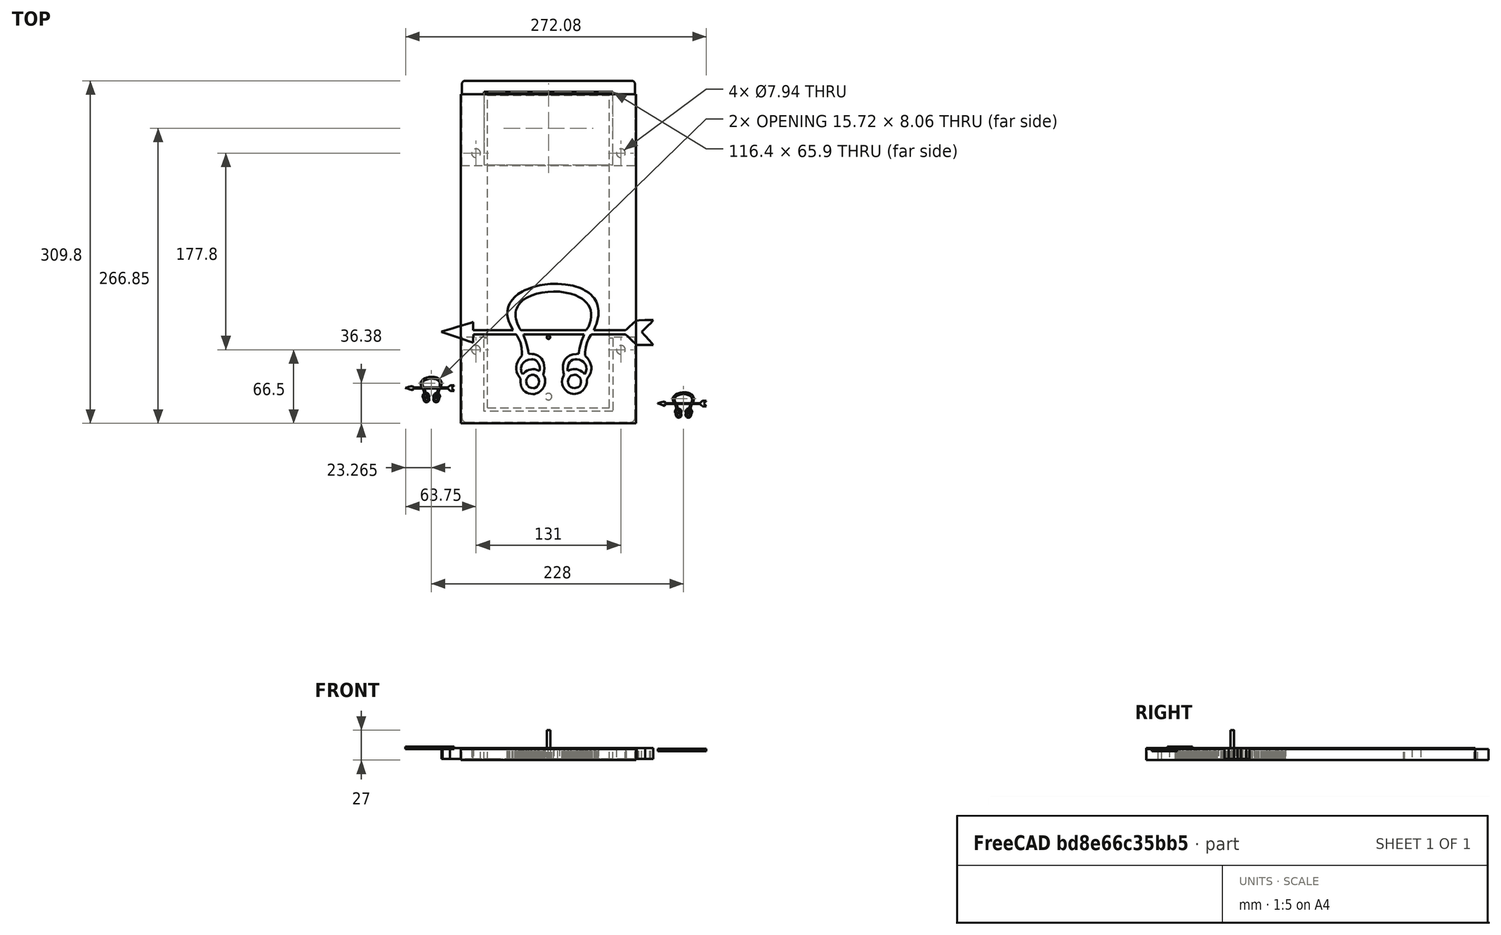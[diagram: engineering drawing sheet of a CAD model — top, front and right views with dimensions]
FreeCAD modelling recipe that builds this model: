
FCSTD DOCUMENT  (FreeCAD 0.22R36958 (Git))
Label: Frame-CNC-center
License: All rights reserved
LicenseURL: http://en.wikipedia.org/wiki/All_rights_reserved
objects: Part::FeaturePython×30, Path::FeaturePython×29, App::DocumentObjectGroup×6, Part::Feature×5, Sketcher::SketchObject×4, PartDesign::Pad×4, PartDesign::Body×4, Part::Part2DObjectPython×2, Part::Extrusion×2, App::FeaturePython×2, Spreadsheet::Sheet×1, Mesh::Feature×1, PartDesign::AdditiveBox×1, PartDesign::SubtractiveCylinder×1, PartDesign::LinearPattern×1
note: 63 computed .brp shape members not serialized (recipe doc carries the construction recipe); baked Part::Feature solids carry a one-line shape summary decoded from their .brp

FEATURE [Part::Part2DObjectPython] ShapeString  # Draft 2D object (typed FeaturePython)
  FontFile = /System/Library/Fonts/Avenir.ttc
  Fuse = false
  Justification = 4
  JustificationReference = 0
  KeepLeftMargin = false
  MakeFace = true
  ObliqueAngle = 0
  Placement = pos=(-68.2,76.9,10) rot=(0,0,1;1.5708rad)
  ScaleToSize = true
  Size = 16
  String = US NAVY
  Tracking = 1
  expr: .Placement.Base.x = -(<<vars>>.width - <<vars>>.top_banner_width) / 2
  expr: .Placement.Base.y = (<<vars>>.length - <<vars>>.template_length) / 2
  expr: .Placement.Base.z = <<vars>>.height
  expr: Size = <<vars>>.font_size
FEATURE [Spreadsheet::Sheet] Spreadsheet  label="vars"
  cells = A1='Length; B1(length)=308.8; C1==B1 / 2; D1='plate hole; E1(plate_hole)=7.9375; A2='Width; B2(width)=156.4; C2=160; D2='plate hole top left distance; E2(plate_hole_vertical)==length / 2 - 177.8 / 2; A3='material length; B3(material_length)=310; D3='plate hole horizontal_right; E3(plate_hole_horizontal_right)==(length - hole_distance_horizontal) / 2; A4='material_width; B4(material_width)=160; D4='plate hole horizontal left; E4(plate_hole_horizontal_left)==length / 2 - 88.9; A5='Font Size; B5(font_size)=16; D5='hole distance horizontal; E5(hole_distance_horizontal)=177.8; A6='Top banner width; B6(top_banner_width)=20; D6='hole distance vertical; E6(hole_distance_vertical)=120.65; A7='Bottom banner witdh; B7(bottom_banner_width)=20; A8='Height; B8(height)=10; A9='Guide hole distance; B9(guide_hole_length)=120; A10='Guide hole width; B10(guide_hole_width)=130; A11='hole distance from edge; B11(hole_distance_from_edge)=20; A12='hole size; B12(hole_size)=6.05; A13='template_length; B13(template_length)=155; A14='reference point; B14(reference_point)==second_cut; C14(second_cut)==(length - template_length) / 2 + template_length; D14(third_cut)==(length - template_length) / 2; E14(first_cut)==length; A15='side_width; B15(side_width)=10; A16='bit size; B16(bit_size)=3.175; A17='bridge width; B17(bridge_width)=1
FEATURE [Part::Part2DObjectPython] ShapeString001  # Draft 2D object (typed FeaturePython)
  FontFile = /System/Library/Fonts/Avenir.ttc
  Fuse = false
  Justification = 4
  JustificationReference = 0
  KeepLeftMargin = false
  MakeFace = true
  ObliqueAngle = 0
  Placement = pos=(68.2,76.9,10) rot=(0,0,1;1.5708rad)
  ScaleToSize = true
  Size = 16
  String = VETERAN
  Tracking = 0
  expr: .Placement.Base.x = (<<vars>>.width - <<vars>>.bottom_banner_width) / 2
  expr: .Placement.Base.y = (<<vars>>.length - <<vars>>.template_length) / 2
  expr: .Placement.Base.z = <<vars>>.height
  expr: Size = <<vars>>.font_size
FEATURE [Mesh::Feature] Sonar_Tech
FEATURE [Part::Feature] Sonar_Tech001
  Placement = pos=(0,0,10) rot=(0,0,1;0rad)
  shape: bbox 191.7 x 99.71 x 10 mm, 1500 faces, 0 solids (baked)
FEATURE [Part::Feature] Shell
  Placement = pos=(0,0,10) rot=(0,0,1;0rad)
  shape: bbox 191.7 x 99.71 x 10 mm, 373 faces, 0 solids (baked)
  expr: .Placement.Base.z = <<vars>>.height
FEATURE [Part::Feature] Scale_solid  label="Scale (Solid)"
  Placement = pos=(13,14,9) rot=(0,0,1;0rad)
  shape: bbox 44.08 x 22.93 x 2.3 mm, 373 faces (baked)
FEATURE [Part::Feature] Scale001_solid  label="Scale001 (Solid)"
  Placement = pos=(0,0,7) rot=(0,0,1;0rad)
  shape: bbox 44.08 x 22.93 x 2.3 mm, 373 faces (baked)
FEATURE [Sketcher::SketchObject] Sketch
  FullyConstrained = true
  MapMode = 5
  expr: Constraints[13] = <<vars>>.width / 2
  expr: Constraints[14] = <<vars>>.width
  expr: Constraints[23] = <<vars>>.top_banner_width
  expr: Constraints[24] = <<vars>>.bottom_banner_width
  expr: Constraints[25] = (<<vars>>.length - <<vars>>.template_length) / 2
  expr: Constraints[29] = <<vars>>.length + 10
  expr: Constraints[30] = (<<vars>>.length - <<vars>>.template_length) / 2 - <<vars>>.side_width - <<vars>>.bridge_width
  expr: Constraints[32] = <<vars>>.plate_hole
  expr: Constraints[33] = <<vars>>.plate_hole
  expr: Constraints[34] = <<vars>>.plate_hole_vertical
  expr: Constraints[35] = <<vars>>.plate_hole_vertical
  expr: Constraints[36] = <<vars>>.plate_hole_horizontal_left
  expr: Constraints[37] = <<vars>>.plate_hole_horizontal_left
  expr: Constraints[38] = <<vars>>.reference_point + 10
  expr: Constraints[39] = <<vars>>.reference_point + <<vars>>.side_width + 10
  sketch-geometry (13):
    g0: LineSegment StartX=78.2 StartY=-5.68e-14 StartZ=0 EndX=-78.2 EndY=-5.68e-14 EndZ=0
    g1: LineSegment StartX=-78.2 StartY=-5.68e-14 StartZ=0 EndX=-78.2 EndY=-72.9 EndZ=0
    g2: ArcOfCircle CenterX=-74.2 CenterY=-72.9 CenterZ=0 NormalX=0 NormalY=0 NormalZ=1 AngleXU=0 Radius=4 StartAngle=3.14159 EndAngle=4.71239
    g3: LineSegment StartX=-74.2 StartY=-76.9 StartZ=0 EndX=74.2 EndY=-76.9 EndZ=0
    g4: ArcOfCircle CenterX=74.2 CenterY=-72.9 CenterZ=0 NormalX=0 NormalY=0 NormalZ=1 AngleXU=0 Radius=4 StartAngle=4.71239 EndAngle=6.28319
    g5: LineSegment StartX=78.2 StartY=-72.9 StartZ=0 EndX=78.2 EndY=-5.68e-14 EndZ=0
    g6: LineSegment StartX=58.2 StartY=-1 StartZ=0 EndX=-58.2 EndY=-1 EndZ=0
    g7: LineSegment StartX=58.2 StartY=-1 StartZ=0 EndX=58.2 EndY=-66.9 EndZ=0
    g8: LineSegment StartX=58.2 StartY=-66.9 StartZ=0 EndX=-58.2 EndY=-66.9 EndZ=0
    g9: LineSegment StartX=-58.2 StartY=-66.9 StartZ=0 EndX=-58.2 EndY=-1 EndZ=0
    g10: GeomPoint X=0 Y=-318.8 Z=0
    g11: Circle CenterX=-65.5 CenterY=-11.4 CenterZ=0 NormalX=0 NormalY=0 NormalZ=1 AngleXU=0 Radius=3.96875
    g12: Circle CenterX=65.5 CenterY=-11.4 CenterZ=0 NormalX=0 NormalY=0 NormalZ=1 AngleXU=0 Radius=3.96875
  constraints (40):
    c: Vertical(g1)
    c: Coincident(g2,g3)
    c: Horizontal(g3)
    c: Tangent(g3,g4) = -1.5708
    c: Coincident(g4,g5)
    c: Vertical(g5)
    c: Horizontal(g8)
    c: Vertical(g9)
    c: Horizontal(g6)
    c: Vertical(g7)
    c: Equal(g2,g4)
    c: Angle(g2) = 1.5708
    c: Angle(g4) = 1.5708
    c: DistanceX(g0,g-1) = 78.2
    c: DistanceX(g0,g5) = 156.4
    c: Equal(g1,g5)
    c: Coincident(g2,g1)
    c: Horizontal(g0)
    c: DistanceX(g2) = -74.2
    c: Coincident(g1,g0)
    c: Coincident(g0,g5)
    c: Coincident(g9,g6)
    c: Coincident(g6,g7)
    c: Distance(g6,g1) = 20
    c: Distance(g6,g5) = 20
    c: Distance(g2,g0) = 76.9
    c: Coincident(g7,g8)
    c: Coincident(g9,g8)
    c: PointOnObject(g10,g-2)
    c: Distance(g-1,g10) = 318.8
    c: DistanceY(g9,g9) = 65.9
    c: DistanceY(g-1,g-1) = 0
    c: Diameter(g11) = 7.9375
    c: Diameter(g12) = 7.9375
    c: DistanceX(g11,g-1) = 65.5
    c: DistanceX(g-1,g12) = 65.5
    c: Distance(g11,g3) = 65.5
    c: Distance(g12,g3) = 65.5
    c: Distance(g10,g3) = 241.9
    c: Distance(g10,g8) = 251.9
FEATURE [PartDesign::Pad] Pad
  Direction = (0,0,1)
  Length = 10
  Length2 = 10
  Profile = -> Sketch
  ReferenceAxis = -> Sketch [N_Axis]
  Suppressed = false
  Type = 0
  expr: Length = <<vars>>.height
FEATURE [PartDesign::AdditiveBox] Box
  AttacherType = Attacher::AttachEngine3D
  AttachmentOffset = pos=(-55.025,-63.725,0) rot=(0,0,1;0rad)
  AttachmentSupport = -> [XY_Plane]
  BaseFeature = -> Pad
  Height = 10
  Length = 110.05
  MapMode = 5
  Placement = pos=(-55.025,-63.725,0) rot=(0,0,1;0rad)
  Suppressed = false
  Width = 282.45
  expr: .AttachmentOffset.Base.x = -<<vars>>.width / 2 + <<vars>>.top_banner_width + <<vars>>.bit_size
  expr: .AttachmentOffset.Base.y = <<vars>>.reference_point - <<vars>>.length + <<vars>>.side_width + <<vars>>.bit_size
  expr: Height = <<vars>>.height
  expr: Length = <<vars>>.width - <<vars>>.top_banner_width - <<vars>>.bottom_banner_width - <<vars>>.bit_size * 2
  expr: Width = <<vars>>.length - <<vars>>.side_width * 2 - <<vars>>.bit_size * 2
FEATURE [Sketcher::SketchObject] Sketch001
  FullyConstrained = true
  MapMode = 5
  expr: Constraints[18] = <<vars>>.width
  expr: Constraints[23] = <<vars>>.top_banner_width
  expr: Constraints[24] = <<vars>>.bottom_banner_width
  expr: Constraints[25] = -<<vars>>.width / 2
  expr: Constraints[26] = (<<vars>>.length - <<vars>>.template_length) / 2
  expr: Constraints[28] = <<vars>>.plate_hole
  expr: Constraints[30] = <<vars>>.plate_hole_vertical
  expr: Constraints[31] = <<vars>>.plate_hole_vertical
  expr: Constraints[32] = <<vars>>.plate_hole_horizontal_right
  expr: Constraints[34] = <<vars>>.length + <<vars>>.reference_point
  expr: Constraints[35] = <<vars>>.length
  expr: Constraints[36] = <<vars>>.length - <<vars>>.side_width + <<vars>>.reference_point
  expr: Constraints[37] = <<vars>>.length - (<<vars>>.length - <<vars>>.template_length) / 2 + <<vars>>.bridge_width + <<vars>>.reference_point
  sketch-geometry (13):
    g0: LineSegment StartX=-78.2 StartY=155 StartZ=0 EndX=-78.2 EndY=228.9 EndZ=0
    g1: ArcOfCircle CenterX=-75.2 CenterY=228.9 CenterZ=0 NormalX=0 NormalY=0 NormalZ=1 AngleXU=0 Radius=3 StartAngle=1.5708 EndAngle=3.14159
    g2: LineSegment StartX=-75.2 StartY=231.9 StartZ=0 EndX=75.2 EndY=231.9 EndZ=0
    g3: ArcOfCircle CenterX=75.2 CenterY=228.9 CenterZ=0 NormalX=0 NormalY=0 NormalZ=1 AngleXU=0 Radius=3 StartAngle=5.988e-13 EndAngle=1.5708
    g4: LineSegment StartX=78.2 StartY=228.9 StartZ=0 EndX=78.2 EndY=155 EndZ=0
    g5: LineSegment StartX=78.2 StartY=155 StartZ=0 EndX=-78.2 EndY=155 EndZ=0
    g6: LineSegment StartX=-58.2 StartY=156 StartZ=0 EndX=58.2 EndY=156 EndZ=0
    g7: LineSegment StartX=58.2 StartY=156 StartZ=0 EndX=58.2 EndY=221.9 EndZ=0
    g8: LineSegment StartX=58.2 StartY=221.9 StartZ=0 EndX=-58.2 EndY=221.9 EndZ=0
    g9: LineSegment StartX=-58.2 StartY=221.9 StartZ=0 EndX=-58.2 EndY=156 EndZ=0
    g10: Circle CenterX=-65.5 CenterY=166.4 CenterZ=0 NormalX=0 NormalY=0 NormalZ=1 AngleXU=0 Radius=3.96875
    g11: Circle CenterX=65.5 CenterY=166.4 CenterZ=0 NormalX=0 NormalY=0 NormalZ=1 AngleXU=0 Radius=3.96875
    g12: GeomPoint X=0 Y=-308.8 Z=0
  constraints (38):
    c: Tangent(g0,g1) = 1.5708
    c: Coincident(g1,g2)
    c: Horizontal(g2)
    c: Tangent(g2,g3) = 1.5708
    c: Coincident(g3,g4)
    c: Vertical(g4)
    c: Coincident(g4,g5)
    c: Coincident(g5,g0)
    c: Horizontal(g5)
    c: Coincident(g6,g7)
    c: Coincident(g7,g8)
    c: Coincident(g8,g9)
    c: Coincident(g9,g6)
    c: Horizontal(g6)
    c: Horizontal(g8)
    c: Vertical(g7)
    c: Vertical(g9)
    c: Vertical(g0)
    c: DistanceX(g5,g5) = 156.4
    c: Angle(g1) = 1.5708
    c: Angle(g3) = 1.5708
    c: Diameter(g1) = 6
    c: Diameter(g3) = 6
    c: Distance(g6,g0) = 20
    c: Distance(g6,g4) = 20
    c: DistanceX(g-2,g0) = -78.2
    c: Distance(g4,g2) = 76.9
    c: Equal(g11,g10)
    c: Diameter(g11) = 7.9375
    c: Horizontal(g10,g11)
    c: DistanceX(g10,g-1) = 65.5
    c: DistanceX(g-1,g11) = 65.5
    c: Distance(g10,g2) = 65.5
    c: PointOnObject(g12,g-2)
    c: Distance(g12,g2) = 540.7
    c: DistanceY(g12,g-1) = 308.8
    c: Distance(g12,g8) = 530.7
    c: Distance(g12,g6) = 464.8
FEATURE [PartDesign::Pad] Pad001
  Direction = (0,0,1)
  Length = 10
  Length2 = 10
  Profile = -> Sketch001
  ReferenceAxis = -> Sketch001 [N_Axis]
  Suppressed = false
  Type = 0
  expr: Length = <<vars>>.height
FEATURE [PartDesign::Body] Body001
  Group = -> [Sketch001,Pad001]
  Origin = -> Origin001
  Tip = -> Pad001
FEATURE [Part::Feature] Sonar_Tech001_solid  label="Sonar_Tech001 (Solid)"
  Placement = pos=(0,0,1) rot=(0,0,1;0rad)
  shape: bbox 191.7 x 99.71 x 10 mm, 1500 faces (baked)
FEATURE [Part::Extrusion] Extrude
  Base = -> ShapeString
  Dir = (0,0,1)
  DirMode = 2
  FaceMakerClass = Part::FaceMakerBullseye
  LengthFwd = 2
  LengthRev = 0
  Solid = false
  Symmetric = true
FEATURE [Part::Extrusion] Extrude001
  Base = -> ShapeString001
  Dir = (0,0,1)
  DirMode = 2
  FaceMakerClass = Part::FaceMakerBullseye
  LengthFwd = 2
  LengthRev = 0
  Solid = false
  Symmetric = true
FEATURE [Sketcher::SketchObject] Sketch002
  FullyConstrained = true
  MapMode = 5
  expr: Constraints[10] = -<<vars>>.width / 2
  expr: Constraints[12] = <<vars>>.length
  expr: Constraints[13] = (<<vars>>.length - <<vars>>.template_length) / 2 + <<vars>>.reference_point
  expr: Constraints[8] = <<vars>>.top_banner_width
  expr: Constraints[9] = <<vars>>.template_length
  sketch-geometry (5):
    g0: LineSegment StartX=-78.2 StartY=155 StartZ=0 EndX=-78.2 EndY=2.84e-14 EndZ=0
    g1: LineSegment StartX=-78.2 StartY=2.13e-14 StartZ=0 EndX=-58.2 EndY=2.13e-14 EndZ=0
    g2: LineSegment StartX=-58.2 StartY=2.13e-14 StartZ=0 EndX=-58.2 EndY=155 EndZ=0
    g3: LineSegment StartX=-58.2 StartY=155 StartZ=0 EndX=-78.2 EndY=155 EndZ=0
    g4: GeomPoint X=0 Y=-308.8 Z=0
  constraints (14):
    c: Coincident(g0,g1)
    c: Coincident(g1,g2)
    c: Coincident(g2,g3)
    c: Coincident(g3,g0)
    c: Vertical(g0)
    c: Vertical(g2)
    c: Horizontal(g1)
    c: Horizontal(g3)
    c: DistanceX(g3,g3) = 20
    c: DistanceY(g0,g0) = 155
    c: DistanceX(g-2,g0) = -78.2
    c: PointOnObject(g4,g-2)
    c: DistanceY(g4,g-1) = 308.8
    c: DistanceY(g4,g1) = 308.8
FEATURE [PartDesign::Pad] Pad002
  Direction = (0,0,1)
  Length = 10
  Length2 = 10
  Profile = -> Sketch002
  ReferenceAxis = -> Sketch002 [N_Axis]
  Suppressed = false
  Type = 0
  expr: Length = <<vars>>.height
FEATURE [PartDesign::Body] Body002
  Group = -> [Sketch002,Pad002]
  Origin = -> Origin002
  Tip = -> Pad002
FEATURE [Sketcher::SketchObject] Sketch003
  FullyConstrained = true
  MapMode = 5
  expr: Constraints[11] = <<vars>>.length
  expr: Constraints[12] = <<vars>>.width / 2
  expr: Constraints[13] = (<<vars>>.length - <<vars>>.template_length) / 2 + <<vars>>.reference_point
  expr: Constraints[8] = <<vars>>.bottom_banner_width
  expr: Constraints[9] = <<vars>>.template_length
  sketch-geometry (5):
    g0: LineSegment StartX=58.2 StartY=155 StartZ=0 EndX=58.2 EndY=0 EndZ=0
    g1: LineSegment StartX=58.2 StartY=1.42e-14 StartZ=0 EndX=78.2 EndY=1.42e-14 EndZ=0
    g2: LineSegment StartX=78.2 StartY=1.42e-14 StartZ=0 EndX=78.2 EndY=155 EndZ=0
    g3: LineSegment StartX=78.2 StartY=155 StartZ=0 EndX=58.2 EndY=155 EndZ=0
    g4: GeomPoint X=0 Y=-308.8 Z=0
  constraints (14):
    c: Coincident(g0,g1)
    c: Coincident(g1,g2)
    c: Coincident(g2,g3)
    c: Coincident(g3,g0)
    c: Vertical(g0)
    c: Vertical(g2)
    c: Horizontal(g1)
    c: Horizontal(g3)
    c: DistanceX(g3,g3) = 20
    c: DistanceY(g2,g2) = 155
    c: PointOnObject(g4,g-2)
    c: DistanceY(g4,g-1) = 308.8
    c: DistanceX(g-1,g2) = 78.2
    c: DistanceY(g4,g0) = 308.8
FEATURE [PartDesign::Pad] Pad003
  Direction = (0,0,1)
  Length = 10
  Length2 = 10
  Profile = -> Sketch003
  ReferenceAxis = -> Sketch003 [N_Axis]
  Suppressed = false
  Type = 0
  expr: Length = <<vars>>.height
FEATURE [PartDesign::Body] Body003
  Group = -> [Sketch003,Pad003]
  Origin = -> Origin003
  Tip = -> Pad003
FEATURE [PartDesign::SubtractiveCylinder] Cylinder
  Angle = 360
  AttacherType = Attacher::AttachEngine3D
  AttachmentOffset = pos=(55.025,10,-10) rot=(0,0,1;0rad)
  AttachmentSupport = -> [Box]
  BaseFeature = -> Box
  FirstAngle = 0
  Height = 10
  MapMode = 5
  Placement = pos=(0,-53.725,0) rot=(0,0,1;0rad)
  Radius = 3.03
  SecondAngle = 0
  Suppressed = false
  expr: .AttachmentOffset.Base.x = Box.Length / 2
  expr: .AttachmentOffset.Base.y = <<vars>>.side_width
  expr: .AttachmentOffset.Base.z = -Height
  expr: Height = <<vars>>.height
  expr: Radius = 3.03
FEATURE [PartDesign::LinearPattern] LinearPattern
  BaseFeature = -> Cylinder
  Direction = -> Y_Axis
  Length = 75.91
  Mode = 1
  Occurrences = 2
  Offset = 75.91
  Originals = -> [Cylinder]
  Placement = pos=(0,-53.725,0) rot=(0,0,1;0rad)
  Suppressed = false
  expr: Offset = 75.91 mm
FEATURE [PartDesign::Body] Body
  Group = -> [Sketch,Pad,Box,Cylinder,LinearPattern]
  Origin = -> Origin
  Tip = -> Cylinder
FEATURE [App::FeaturePython] SetupSheet  # Path/CAM operation (typed FeaturePython)
  ClearanceHeightExpression = OpStockZMax+SetupSheet.ClearanceHeightOffset
  ClearanceHeightOffset = 5
  CoolantMode = 0
  CoolantModes = None | Flood | Mist
  FinalDepthExpression = OpFinalDepth
  HorizRapid = 0
  SafeHeightExpression = OpStockZMax+SetupSheet.SafeHeightOffset
  SafeHeightOffset = 3
  StartDepthExpression = OpStartDepth
  StepDownExpression = OpToolDiameter
  VertRapid = 0
FEATURE [Part::FeaturePython] Clone  label="Model-Body"  # Draft clone (typed FeaturePython)
  AttacherType = Attacher::AttachEngine3D
  Fuse = false
  Objects = -> [Body]
  PathResource = Model
  Scale = (1,1,1)
FEATURE [Part::FeaturePython] Clone001  label="Model-Extrude"  # Draft clone (typed FeaturePython)
  AttacherType = Attacher::AttachEngine3D
  Fuse = false
  Objects = -> [Extrude]
  PathResource = Model
  Scale = (1,1,1)
FEATURE [Part::FeaturePython] Clone002  label="Model-Extrude001"  # Draft clone (typed FeaturePython)
  AttacherType = Attacher::AttachEngine3D
  Fuse = false
  Objects = -> [Extrude001]
  PathResource = Model
  Scale = (1,1,1)
FEATURE [App::DocumentObjectGroup] Model
  Group = -> [Clone,Clone001,Clone002]
FEATURE [Part::FeaturePython] ToolBit  label="0.8mm_Endmill004"  # Path/CAM toolbit (typed FeaturePython)
  BitPropertyNames = Chipload | CuttingEdgeHeight | Diameter | Flutes | Length | Material | ShankDiameter | SpindleDirection
  BitShape = /private/var/folders/4z/cpn_82wx3qz0m4lfqxz9fps80000gn/T/AppTranslocation/590B87E8-BEDD-40D1-A770-7063B047F674/d/FreeCAD.app/Contents/Resources/Mod/CAM/Tools/Shape/endmill.fcstd
  Chipload = 0
  CuttingEdgeHeight = 10
  Diameter = 0.8
  Flutes = 0
  Length = 27
  Material = 0
  ShankDiameter = 3.17
  ShapeName = endmill
  SpindleDirection = 0
FEATURE [Path::FeaturePython] __8mm_Endmill001  label="0.8mm_Endmill002"  # Path/CAM operation (typed FeaturePython)
  HorizFeed = 3.33333
  HorizRapid = 0
  SpindleDir = 0
  SpindleSpeed = 2000
  Tool = -> ToolBit
  ToolNumber = 2
  VertFeed = 3.33333
  VertRapid = 0
  expr: HorizRapid = SetupSheet.HorizRapid
  expr: VertRapid = SetupSheet.VertRapid
FEATURE [Part::FeaturePython] ToolBit001  label="1.0mm_Endmill003"  # Path/CAM toolbit (typed FeaturePython)
  BitPropertyNames = Chipload | CuttingEdgeHeight | Diameter | Flutes | Length | Material | ShankDiameter | SpindleDirection
  BitShape = /private/var/folders/4z/cpn_82wx3qz0m4lfqxz9fps80000gn/T/AppTranslocation/590B87E8-BEDD-40D1-A770-7063B047F674/d/FreeCAD.app/Contents/Resources/Mod/CAM/Tools/Shape/endmill.fcstd
  Chipload = 0
  CuttingEdgeHeight = 10
  Diameter = 1
  Flutes = 0
  Length = 27
  Material = 0
  ShankDiameter = 3.17
  ShapeName = endmill
  SpindleDirection = 0
FEATURE [Path::FeaturePython] __0mm_Endmill001  label="1.0mm_Endmill002"  # Path/CAM operation (typed FeaturePython)
  HorizFeed = 3.33333
  HorizRapid = 0
  SpindleDir = 0
  SpindleSpeed = 2000
  Tool = -> ToolBit001
  ToolNumber = 3
  VertFeed = 3.33333
  VertRapid = 0
  expr: HorizRapid = SetupSheet.HorizRapid
  expr: VertRapid = SetupSheet.VertRapid
FEATURE [Part::FeaturePython] ToolBit002  label="1.2mm_endmill003"  # Path/CAM toolbit (typed FeaturePython)
  BitPropertyNames = Chipload | CuttingEdgeHeight | Diameter | Flutes | Length | Material | ShankDiameter | SpindleDirection
  BitShape = /private/var/folders/4z/cpn_82wx3qz0m4lfqxz9fps80000gn/T/AppTranslocation/590B87E8-BEDD-40D1-A770-7063B047F674/d/FreeCAD.app/Contents/Resources/Mod/CAM/Tools/Shape/endmill.fcstd
  Chipload = 0
  CuttingEdgeHeight = 10
  Diameter = 1.2
  Flutes = 0
  Length = 27
  Material = 0
  ShankDiameter = 3.13
  ShapeName = endmill
  SpindleDirection = 0
FEATURE [Path::FeaturePython] __2mm_endmill001  label="1.2mm_endmill002"  # Path/CAM operation (typed FeaturePython)
  HorizFeed = 3.33333
  HorizRapid = 0
  SpindleDir = 0
  SpindleSpeed = 2000
  Tool = -> ToolBit002
  ToolNumber = 4
  VertFeed = 3.33333
  VertRapid = 0
  expr: HorizRapid = SetupSheet.HorizRapid
  expr: VertRapid = SetupSheet.VertRapid
FEATURE [Part::FeaturePython] ToolBit003  label="1.4mm_Endmill003"  # Path/CAM toolbit (typed FeaturePython)
  BitPropertyNames = Chipload | CuttingEdgeHeight | Diameter | Flutes | Length | Material | ShankDiameter | SpindleDirection
  BitShape = /private/var/folders/4z/cpn_82wx3qz0m4lfqxz9fps80000gn/T/AppTranslocation/590B87E8-BEDD-40D1-A770-7063B047F674/d/FreeCAD.app/Contents/Resources/Mod/CAM/Tools/Shape/endmill.fcstd
  Chipload = 0
  CuttingEdgeHeight = 10
  Diameter = 1.4
  Flutes = 0
  Length = 27
  Material = 0
  ShankDiameter = 3.17
  ShapeName = endmill
  SpindleDirection = 0
FEATURE [Path::FeaturePython] __4mm_Endmill001  label="1.4mm_Endmill002"  # Path/CAM operation (typed FeaturePython)
  HorizFeed = 3.33333
  HorizRapid = 0
  SpindleDir = 0
  SpindleSpeed = 2000
  Tool = -> ToolBit003
  ToolNumber = 5
  VertFeed = 3.33333
  VertRapid = 0
  expr: HorizRapid = SetupSheet.HorizRapid
  expr: VertRapid = SetupSheet.VertRapid
FEATURE [Part::FeaturePython] ToolBit004  label="1.8mm_Endmill"  # Path/CAM toolbit (typed FeaturePython)
  BitPropertyNames = Chipload | CuttingEdgeHeight | Diameter | Flutes | Length | Material | ShankDiameter | SpindleDirection
  BitShape = /private/var/folders/4z/cpn_82wx3qz0m4lfqxz9fps80000gn/T/AppTranslocation/590B87E8-BEDD-40D1-A770-7063B047F674/d/FreeCAD.app/Contents/Resources/Mod/CAM/Tools/Shape/endmill.fcstd
  Chipload = 0
  CuttingEdgeHeight = 10
  Diameter = 1.8
  Flutes = 0
  Length = 27
  Material = 0
  ShankDiameter = 3.17
  ShapeName = endmill
  SpindleDirection = 0
FEATURE [Path::FeaturePython] __8mm_Endmill002  label="1.8mm_Endmill001"  # Path/CAM operation (typed FeaturePython)
  HorizFeed = 3.33333
  HorizRapid = 0
  SpindleDir = 0
  SpindleSpeed = 2000
  Tool = -> ToolBit004
  ToolNumber = 7
  VertFeed = 3.33333
  VertRapid = 0
  expr: HorizRapid = SetupSheet.HorizRapid
  expr: VertRapid = SetupSheet.VertRapid
FEATURE [Part::FeaturePython] ToolBit005  label="2.0mm_Endmill"  # Path/CAM toolbit (typed FeaturePython)
  BitPropertyNames = Chipload | CuttingEdgeHeight | Diameter | Flutes | Length | Material | ShankDiameter | SpindleDirection
  BitShape = /private/var/folders/4z/cpn_82wx3qz0m4lfqxz9fps80000gn/T/AppTranslocation/590B87E8-BEDD-40D1-A770-7063B047F674/d/FreeCAD.app/Contents/Resources/Mod/CAM/Tools/Shape/endmill.fcstd
  Chipload = 0
  CuttingEdgeHeight = 10
  Diameter = 2
  Flutes = 0
  Length = 27
  Material = 0
  ShankDiameter = 3.17
  ShapeName = endmill
  SpindleDirection = 0
FEATURE [Path::FeaturePython] __0mm_Endmill002  label="2.0mm_Endmill001"  # Path/CAM operation (typed FeaturePython)
  HorizFeed = 3.33333
  HorizRapid = 0
  SpindleDir = 0
  SpindleSpeed = 2000
  Tool = -> ToolBit005
  ToolNumber = 8
  VertFeed = 3.33333
  VertRapid = 0
  expr: HorizRapid = SetupSheet.HorizRapid
  expr: VertRapid = SetupSheet.VertRapid
FEATURE [Part::FeaturePython] ToolBit006  label="2.2mm_Endmill"  # Path/CAM toolbit (typed FeaturePython)
  BitPropertyNames = Chipload | CuttingEdgeHeight | Diameter | Flutes | Length | Material | ShankDiameter | SpindleDirection
  BitShape = /private/var/folders/4z/cpn_82wx3qz0m4lfqxz9fps80000gn/T/AppTranslocation/590B87E8-BEDD-40D1-A770-7063B047F674/d/FreeCAD.app/Contents/Resources/Mod/CAM/Tools/Shape/endmill.fcstd
  Chipload = 0
  CuttingEdgeHeight = 10
  Diameter = 2.2
  Flutes = 0
  Length = 27
  Material = 0
  ShankDiameter = 3.17
  ShapeName = endmill
  SpindleDirection = 0
FEATURE [Path::FeaturePython] __2mm_Endmill  label="2.2mm_Endmill001"  # Path/CAM operation (typed FeaturePython)
  HorizFeed = 3.33333
  HorizRapid = 0
  SpindleDir = 0
  SpindleSpeed = 2000
  Tool = -> ToolBit006
  ToolNumber = 9
  VertFeed = 3.33333
  VertRapid = 0
  expr: HorizRapid = SetupSheet.HorizRapid
  expr: VertRapid = SetupSheet.VertRapid
FEATURE [Part::FeaturePython] ToolBit007  label="2.4mm_Endmill"  # Path/CAM toolbit (typed FeaturePython)
  BitPropertyNames = Chipload | CuttingEdgeHeight | Diameter | Flutes | Length | Material | ShankDiameter | SpindleDirection
  BitShape = /private/var/folders/4z/cpn_82wx3qz0m4lfqxz9fps80000gn/T/AppTranslocation/590B87E8-BEDD-40D1-A770-7063B047F674/d/FreeCAD.app/Contents/Resources/Mod/CAM/Tools/Shape/endmill.fcstd
  Chipload = 0
  CuttingEdgeHeight = 10
  Diameter = 2.4
  Flutes = 0
  Length = 27
  Material = 0
  ShankDiameter = 3.17
  ShapeName = endmill
  SpindleDirection = 0
FEATURE [Path::FeaturePython] __4mm_Endmill002  label="2.4mm_Endmill001"  # Path/CAM operation (typed FeaturePython)
  HorizFeed = 3.33333
  HorizRapid = 0
  SpindleDir = 0
  SpindleSpeed = 2000
  Tool = -> ToolBit007
  ToolNumber = 10
  VertFeed = 3.33333
  VertRapid = 0
  expr: HorizRapid = SetupSheet.HorizRapid
  expr: VertRapid = SetupSheet.VertRapid
FEATURE [Part::FeaturePython] ToolBit008  label="2.6mm_Endmill"  # Path/CAM toolbit (typed FeaturePython)
  BitPropertyNames = Chipload | CuttingEdgeHeight | Diameter | Flutes | Length | Material | ShankDiameter | SpindleDirection
  BitShape = /private/var/folders/4z/cpn_82wx3qz0m4lfqxz9fps80000gn/T/AppTranslocation/590B87E8-BEDD-40D1-A770-7063B047F674/d/FreeCAD.app/Contents/Resources/Mod/CAM/Tools/Shape/endmill.fcstd
  Chipload = 0
  CuttingEdgeHeight = 10
  Diameter = 2.6
  Flutes = 0
  Length = 27
  Material = 0
  ShankDiameter = 3.17
  ShapeName = endmill
  SpindleDirection = 0
FEATURE [Path::FeaturePython] __6mm_Endmill  label="2.6mm_Endmill001"  # Path/CAM operation (typed FeaturePython)
  HorizFeed = 3.33333
  HorizRapid = 0
  SpindleDir = 0
  SpindleSpeed = 2000
  Tool = -> ToolBit008
  ToolNumber = 11
  VertFeed = 3.33333
  VertRapid = 0
  expr: HorizRapid = SetupSheet.HorizRapid
  expr: VertRapid = SetupSheet.VertRapid
FEATURE [Part::FeaturePython] ToolBit009  label="2.8mm_Endmill"  # Path/CAM toolbit (typed FeaturePython)
  BitPropertyNames = Chipload | CuttingEdgeHeight | Diameter | Flutes | Length | Material | ShankDiameter | SpindleDirection
  BitShape = /private/var/folders/4z/cpn_82wx3qz0m4lfqxz9fps80000gn/T/AppTranslocation/590B87E8-BEDD-40D1-A770-7063B047F674/d/FreeCAD.app/Contents/Resources/Mod/CAM/Tools/Shape/endmill.fcstd
  Chipload = 0
  CuttingEdgeHeight = 10
  Diameter = 2.8
  Flutes = 0
  Length = 27
  Material = 0
  ShankDiameter = 3.17
  ShapeName = endmill
  SpindleDirection = 0
FEATURE [Path::FeaturePython] __8mm_Endmill003  label="2.8mm_Endmill001"  # Path/CAM operation (typed FeaturePython)
  HorizFeed = 3.33333
  HorizRapid = 0
  SpindleDir = 0
  SpindleSpeed = 2000
  Tool = -> ToolBit009
  ToolNumber = 12
  VertFeed = 3.33333
  VertRapid = 0
  expr: HorizRapid = SetupSheet.HorizRapid
  expr: VertRapid = SetupSheet.VertRapid
FEATURE [Part::FeaturePython] ToolBit010  label="3.0mm_Endmill"  # Path/CAM toolbit (typed FeaturePython)
  BitPropertyNames = Chipload | CuttingEdgeHeight | Diameter | Flutes | Length | Material | ShankDiameter | SpindleDirection
  BitShape = /private/var/folders/4z/cpn_82wx3qz0m4lfqxz9fps80000gn/T/AppTranslocation/590B87E8-BEDD-40D1-A770-7063B047F674/d/FreeCAD.app/Contents/Resources/Mod/CAM/Tools/Shape/endmill.fcstd
  Chipload = 0
  CuttingEdgeHeight = 10
  Diameter = 3
  Flutes = 0
  Length = 27
  Material = 0
  ShankDiameter = 3.17
  ShapeName = endmill
  SpindleDirection = 0
FEATURE [Path::FeaturePython] __0mm_Endmill003  label="3.0mm_Endmill001"  # Path/CAM operation (typed FeaturePython)
  HorizFeed = 3.33333
  HorizRapid = 0
  SpindleDir = 0
  SpindleSpeed = 2000
  Tool = -> ToolBit010
  ToolNumber = 13
  VertFeed = 3.33333
  VertRapid = 0
  expr: HorizRapid = SetupSheet.HorizRapid
  expr: VertRapid = SetupSheet.VertRapid
FEATURE [Part::FeaturePython] ToolBit011  label="3.175mm_endmill009"  # Path/CAM toolbit (typed FeaturePython)
  BitPropertyNames = Chipload | CuttingEdgeHeight | Diameter | Flutes | Length | Material | ShankDiameter | SpindleDirection
  BitShape = /private/var/folders/4z/cpn_82wx3qz0m4lfqxz9fps80000gn/T/AppTranslocation/590B87E8-BEDD-40D1-A770-7063B047F674/d/FreeCAD.app/Contents/Resources/Mod/CAM/Tools/Shape/endmill.fcstd
  Chipload = 0
  CuttingEdgeHeight = 10
  Diameter = 3.17
  Flutes = 0
  Length = 27
  Material = 0
  ShankDiameter = 3.17
  ShapeName = endmill
  SpindleDirection = 0
FEATURE [Path::FeaturePython] __175mm_endmill007  label="3.175mm_endmill008"  # Path/CAM operation (typed FeaturePython)
  HorizFeed = 3.33333
  HorizRapid = 0
  SpindleDir = 0
  SpindleSpeed = 2000
  Tool = -> ToolBit011
  ToolNumber = 6
  VertFeed = 3.33333
  VertRapid = 0
  expr: HorizRapid = SetupSheet.HorizRapid
  expr: VertRapid = SetupSheet.VertRapid
FEATURE [App::DocumentObjectGroup] Tools
  Group = -> [__8mm_Endmill001,__0mm_Endmill001,__2mm_endmill001,__4mm_Endmill001,__8mm_Endmill002,__0mm_Endmill002,__2mm_Endmill,__4mm_Endmill002,__6mm_Endmill,__8mm_Endmill003,__0mm_Endmill003,__175mm_endmill007]
FEATURE [Part::FeaturePython] Stock  # WARN: FeaturePython — macro-defined, semantics opaque (R4)
  Base = -> Model
  ExtXneg = 1
  ExtXpos = 1
  ExtYneg = 1
  ExtYpos = 1
  ExtZneg = 0
  ExtZpos = 0
  Placement = pos=(-78.2,-76.9,0) rot=(0,0,1;0rad)
  StockType = FromBase
FEATURE [Path::FeaturePython] Pocket_Shape  # Path/CAM operation (typed FeaturePython)
  Active = true
  AreaParams:
    Tolerance = 1e-07
    FitArcs = True
    Simplify = False
    CleanDistance = 0.0
    Accuracy = 0.01
    Unit = 1.0
    MinArcPoints = 4
    MaxArcPoints = 100
    ClipperScale = 10000000.0
    Fill = 0
    Coplanar = 0
    Reorient = True
    Outline = False
    Explode = False
    OpenMode = 0
    Deflection = 0.01
    SubjectFill = 0
    ClipFill = 0
    Offset = 0.0
    ExtraPass = 0
    Stepover = 0.0
    LastStepover = 0.0
    JoinType = 0
    EndType = 0
    MiterLimit = 2.0
    RoundPrecision = 0.0
    PocketMode = 2
    ToolRadius = 0.4
    PocketExtraOffset = 0.0
    PocketStepover = 0.8
    PocketLastStepover = 0.0
    FromCenter = True
    Angle = 45.0
    AngleShift = 0.0
    Shift = 0.0
    Thicken = False
    SectionCount = -1
    Stepdown = 1.0
    SectionOffset = 0.0
    SectionTolerance = 1e-06
    SectionMode = 2
    Project = False
  Base = -> [Clone001,Clone002]
  ClearanceHeight = 16
  CoolantMode = 0
  CutMode = 0
  CycleTime = 01:06:36
  ExtensionCorners = true
  ExtensionLengthDefault = 0.4
  ExtraOffset = 0
  FinalDepth = 8
  FinishDepth = 0
  KeepToolDown = false
  MinTravel = true
  OffsetPattern = 1
  OpFinalDepth = 11
  OpStartDepth = 11.8
  OpStockZMax = 11
  OpStockZMin = 0
  OpToolDiameter = 0.8
  PathParams = {'orientation': 1, 'feedrate': 3.3333333333333335, 'feedrate_v': 3.3333333333333335, 'verbose': True, 'resume_height': 14.0, 'retraction': 16.0, 'return_end': True, 'preamble': False, 'start': Vector (61.00000009999997, 45.212195023529425, 16.0)}
  PocketLastStepOver = 0
  SafeHeight = 14
  SplitArcs = false
  StartAt = 0
  StartDepth = 11.8
  StartPoint = (0,0,0)
  StepDown = 0.8
  StepOver = 100
  ToolController = -> __8mm_Endmill001
  UseOutline = false
  UseRestMachining = false
  UseStartPoint = false
  ZigZagAngle = 45
  expr: ClearanceHeight = OpStockZMax + SetupSheet.ClearanceHeightOffset
  expr: ExtensionLengthDefault = OpToolDiameter / 2
  expr: FinalDepth = 8
  expr: SafeHeight = OpStockZMax + SetupSheet.SafeHeightOffset
  expr: StartDepth = OpStartDepth
  expr: StepDown = OpToolDiameter
FEATURE [App::DocumentObjectGroup] Operations
  Group = -> [Pocket_Shape]
FEATURE [Path::FeaturePython] Job  # Path/CAM operation (typed FeaturePython)
  CycleTime = 01:06:36
  Fixtures = G54
  GeometryTolerance = 0.01
  JobType = 0
  Model = -> Model
  Operations = -> Operations
  OrderOutputBy = 0
  PostProcessor = 1
  SetupSheet = -> SetupSheet
  SplitOutput = false
  Stock = -> Stock
  Tools = -> Tools
FEATURE [App::FeaturePython] SetupSheet001  # Path/CAM operation (typed FeaturePython)
  ClearanceHeightExpression = OpStockZMax+SetupSheet001.ClearanceHeightOffset
  ClearanceHeightOffset = 5
  CoolantMode = 0
  CoolantModes = None | Flood | Mist
  FinalDepthExpression = OpFinalDepth
  HorizRapid = 0
  SafeHeightExpression = OpStockZMax+SetupSheet001.SafeHeightOffset
  SafeHeightOffset = 3
  StartDepthExpression = OpStartDepth
  StepDownExpression = OpToolDiameter
  VertRapid = 0
FEATURE [Part::FeaturePython] Clone003  label="Model-Body001"  # Draft clone (typed FeaturePython)
  AttacherType = Attacher::AttachEngine3D
  Fuse = false
  Objects = -> [Body]
  PathResource = Model
  Scale = (1,1,1)
FEATURE [App::DocumentObjectGroup] Model001
  Group = -> [Clone003]
FEATURE [Part::FeaturePython] ToolBit012  label="0.8mm_Endmill006"  # Path/CAM toolbit (typed FeaturePython)
  BitPropertyNames = Chipload | CuttingEdgeHeight | Diameter | Flutes | Length | Material | ShankDiameter | SpindleDirection
  BitShape = /private/var/folders/4z/cpn_82wx3qz0m4lfqxz9fps80000gn/T/AppTranslocation/590B87E8-BEDD-40D1-A770-7063B047F674/d/FreeCAD.app/Contents/Resources/Mod/CAM/Tools/Shape/endmill.fcstd
  Chipload = 0
  CuttingEdgeHeight = 10
  Diameter = 0.8
  Flutes = 0
  Length = 27
  Material = 0
  ShankDiameter = 3.17
  ShapeName = endmill
  SpindleDirection = 0
FEATURE [Path::FeaturePython] __8mm_Endmill004  label="0.8mm_Endmill005"  # Path/CAM operation (typed FeaturePython)
  HorizFeed = 3.33333
  HorizRapid = 0
  SpindleDir = 0
  SpindleSpeed = 2000
  Tool = -> ToolBit012
  ToolNumber = 2
  VertFeed = 3.33333
  VertRapid = 0
  expr: HorizRapid = SetupSheet001.HorizRapid
  expr: VertRapid = SetupSheet001.VertRapid
FEATURE [Part::FeaturePython] ToolBit013  label="1.0mm_Endmill005"  # Path/CAM toolbit (typed FeaturePython)
  BitPropertyNames = Chipload | CuttingEdgeHeight | Diameter | Flutes | Length | Material | ShankDiameter | SpindleDirection
  BitShape = /private/var/folders/4z/cpn_82wx3qz0m4lfqxz9fps80000gn/T/AppTranslocation/590B87E8-BEDD-40D1-A770-7063B047F674/d/FreeCAD.app/Contents/Resources/Mod/CAM/Tools/Shape/endmill.fcstd
  Chipload = 0
  CuttingEdgeHeight = 10
  Diameter = 1
  Flutes = 0
  Length = 27
  Material = 0
  ShankDiameter = 3.17
  ShapeName = endmill
  SpindleDirection = 0
FEATURE [Path::FeaturePython] __0mm_Endmill004  label="1.0mm_Endmill004"  # Path/CAM operation (typed FeaturePython)
  HorizFeed = 3.33333
  HorizRapid = 0
  SpindleDir = 0
  SpindleSpeed = 2000
  Tool = -> ToolBit013
  ToolNumber = 3
  VertFeed = 3.33333
  VertRapid = 0
  expr: HorizRapid = SetupSheet001.HorizRapid
  expr: VertRapid = SetupSheet001.VertRapid
FEATURE [Part::FeaturePython] ToolBit014  label="1.2mm_endmill005"  # Path/CAM toolbit (typed FeaturePython)
  BitPropertyNames = Chipload | CuttingEdgeHeight | Diameter | Flutes | Length | Material | ShankDiameter | SpindleDirection
  BitShape = /private/var/folders/4z/cpn_82wx3qz0m4lfqxz9fps80000gn/T/AppTranslocation/590B87E8-BEDD-40D1-A770-7063B047F674/d/FreeCAD.app/Contents/Resources/Mod/CAM/Tools/Shape/endmill.fcstd
  Chipload = 0
  CuttingEdgeHeight = 10
  Diameter = 1.2
  Flutes = 0
  Length = 27
  Material = 0
  ShankDiameter = 3.13
  ShapeName = endmill
  SpindleDirection = 0
FEATURE [Path::FeaturePython] __2mm_endmill002  label="1.2mm_endmill004"  # Path/CAM operation (typed FeaturePython)
  HorizFeed = 3.33333
  HorizRapid = 0
  SpindleDir = 0
  SpindleSpeed = 2000
  Tool = -> ToolBit014
  ToolNumber = 4
  VertFeed = 3.33333
  VertRapid = 0
  expr: HorizRapid = SetupSheet001.HorizRapid
  expr: VertRapid = SetupSheet001.VertRapid
FEATURE [Part::FeaturePython] ToolBit015  label="1.4mm_Endmill005"  # Path/CAM toolbit (typed FeaturePython)
  BitPropertyNames = Chipload | CuttingEdgeHeight | Diameter | Flutes | Length | Material | ShankDiameter | SpindleDirection
  BitShape = /private/var/folders/4z/cpn_82wx3qz0m4lfqxz9fps80000gn/T/AppTranslocation/590B87E8-BEDD-40D1-A770-7063B047F674/d/FreeCAD.app/Contents/Resources/Mod/CAM/Tools/Shape/endmill.fcstd
  Chipload = 0
  CuttingEdgeHeight = 10
  Diameter = 1.4
  Flutes = 0
  Length = 27
  Material = 0
  ShankDiameter = 3.17
  ShapeName = endmill
  SpindleDirection = 0
FEATURE [Path::FeaturePython] __4mm_Endmill003  label="1.4mm_Endmill004"  # Path/CAM operation (typed FeaturePython)
  HorizFeed = 3.33333
  HorizRapid = 0
  SpindleDir = 0
  SpindleSpeed = 2000
  Tool = -> ToolBit015
  ToolNumber = 5
  VertFeed = 3.33333
  VertRapid = 0
  expr: HorizRapid = SetupSheet001.HorizRapid
  expr: VertRapid = SetupSheet001.VertRapid
FEATURE [Part::FeaturePython] ToolBit016  label="1.8mm_Endmill003"  # Path/CAM toolbit (typed FeaturePython)
  BitPropertyNames = Chipload | CuttingEdgeHeight | Diameter | Flutes | Length | Material | ShankDiameter | SpindleDirection
  BitShape = /private/var/folders/4z/cpn_82wx3qz0m4lfqxz9fps80000gn/T/AppTranslocation/590B87E8-BEDD-40D1-A770-7063B047F674/d/FreeCAD.app/Contents/Resources/Mod/CAM/Tools/Shape/endmill.fcstd
  Chipload = 0
  CuttingEdgeHeight = 10
  Diameter = 1.8
  Flutes = 0
  Length = 27
  Material = 0
  ShankDiameter = 3.17
  ShapeName = endmill
  SpindleDirection = 0
FEATURE [Path::FeaturePython] __8mm_Endmill005  label="1.8mm_Endmill002"  # Path/CAM operation (typed FeaturePython)
  HorizFeed = 3.33333
  HorizRapid = 0
  SpindleDir = 0
  SpindleSpeed = 2000
  Tool = -> ToolBit016
  ToolNumber = 7
  VertFeed = 3.33333
  VertRapid = 0
  expr: HorizRapid = SetupSheet001.HorizRapid
  expr: VertRapid = SetupSheet001.VertRapid
FEATURE [Part::FeaturePython] ToolBit017  label="2.0mm_Endmill003"  # Path/CAM toolbit (typed FeaturePython)
  BitPropertyNames = Chipload | CuttingEdgeHeight | Diameter | Flutes | Length | Material | ShankDiameter | SpindleDirection
  BitShape = /private/var/folders/4z/cpn_82wx3qz0m4lfqxz9fps80000gn/T/AppTranslocation/590B87E8-BEDD-40D1-A770-7063B047F674/d/FreeCAD.app/Contents/Resources/Mod/CAM/Tools/Shape/endmill.fcstd
  Chipload = 0
  CuttingEdgeHeight = 10
  Diameter = 2
  Flutes = 0
  Length = 27
  Material = 0
  ShankDiameter = 3.17
  ShapeName = endmill
  SpindleDirection = 0
FEATURE [Path::FeaturePython] __0mm_Endmill005  label="2.0mm_Endmill002"  # Path/CAM operation (typed FeaturePython)
  HorizFeed = 3.33333
  HorizRapid = 0
  SpindleDir = 0
  SpindleSpeed = 2000
  Tool = -> ToolBit017
  ToolNumber = 8
  VertFeed = 3.33333
  VertRapid = 0
  expr: HorizRapid = SetupSheet001.HorizRapid
  expr: VertRapid = SetupSheet001.VertRapid
FEATURE [Part::FeaturePython] ToolBit018  label="2.2mm_Endmill003"  # Path/CAM toolbit (typed FeaturePython)
  BitPropertyNames = Chipload | CuttingEdgeHeight | Diameter | Flutes | Length | Material | ShankDiameter | SpindleDirection
  BitShape = /private/var/folders/4z/cpn_82wx3qz0m4lfqxz9fps80000gn/T/AppTranslocation/590B87E8-BEDD-40D1-A770-7063B047F674/d/FreeCAD.app/Contents/Resources/Mod/CAM/Tools/Shape/endmill.fcstd
  Chipload = 0
  CuttingEdgeHeight = 10
  Diameter = 2.2
  Flutes = 0
  Length = 27
  Material = 0
  ShankDiameter = 3.17
  ShapeName = endmill
  SpindleDirection = 0
FEATURE [Path::FeaturePython] __2mm_Endmill001  label="2.2mm_Endmill002"  # Path/CAM operation (typed FeaturePython)
  HorizFeed = 3.33333
  HorizRapid = 0
  SpindleDir = 0
  SpindleSpeed = 2000
  Tool = -> ToolBit018
  ToolNumber = 9
  VertFeed = 3.33333
  VertRapid = 0
  expr: HorizRapid = SetupSheet001.HorizRapid
  expr: VertRapid = SetupSheet001.VertRapid
FEATURE [Part::FeaturePython] ToolBit019  label="2.4mm_Endmill003"  # Path/CAM toolbit (typed FeaturePython)
  BitPropertyNames = Chipload | CuttingEdgeHeight | Diameter | Flutes | Length | Material | ShankDiameter | SpindleDirection
  BitShape = /private/var/folders/4z/cpn_82wx3qz0m4lfqxz9fps80000gn/T/AppTranslocation/590B87E8-BEDD-40D1-A770-7063B047F674/d/FreeCAD.app/Contents/Resources/Mod/CAM/Tools/Shape/endmill.fcstd
  Chipload = 0
  CuttingEdgeHeight = 10
  Diameter = 2.4
  Flutes = 0
  Length = 27
  Material = 0
  ShankDiameter = 3.17
  ShapeName = endmill
  SpindleDirection = 0
FEATURE [Path::FeaturePython] __4mm_Endmill004  label="2.4mm_Endmill002"  # Path/CAM operation (typed FeaturePython)
  HorizFeed = 3.33333
  HorizRapid = 0
  SpindleDir = 0
  SpindleSpeed = 2000
  Tool = -> ToolBit019
  ToolNumber = 10
  VertFeed = 3.33333
  VertRapid = 0
  expr: HorizRapid = SetupSheet001.HorizRapid
  expr: VertRapid = SetupSheet001.VertRapid
FEATURE [Part::FeaturePython] ToolBit020  label="2.6mm_Endmill003"  # Path/CAM toolbit (typed FeaturePython)
  BitPropertyNames = Chipload | CuttingEdgeHeight | Diameter | Flutes | Length | Material | ShankDiameter | SpindleDirection
  BitShape = /private/var/folders/4z/cpn_82wx3qz0m4lfqxz9fps80000gn/T/AppTranslocation/590B87E8-BEDD-40D1-A770-7063B047F674/d/FreeCAD.app/Contents/Resources/Mod/CAM/Tools/Shape/endmill.fcstd
  Chipload = 0
  CuttingEdgeHeight = 10
  Diameter = 2.6
  Flutes = 0
  Length = 27
  Material = 0
  ShankDiameter = 3.17
  ShapeName = endmill
  SpindleDirection = 0
FEATURE [Path::FeaturePython] __6mm_Endmill001  label="2.6mm_Endmill002"  # Path/CAM operation (typed FeaturePython)
  HorizFeed = 3.33333
  HorizRapid = 0
  SpindleDir = 0
  SpindleSpeed = 2000
  Tool = -> ToolBit020
  ToolNumber = 11
  VertFeed = 3.33333
  VertRapid = 0
  expr: HorizRapid = SetupSheet001.HorizRapid
  expr: VertRapid = SetupSheet001.VertRapid
FEATURE [Part::FeaturePython] ToolBit021  label="2.8mm_Endmill003"  # Path/CAM toolbit (typed FeaturePython)
  BitPropertyNames = Chipload | CuttingEdgeHeight | Diameter | Flutes | Length | Material | ShankDiameter | SpindleDirection
  BitShape = /private/var/folders/4z/cpn_82wx3qz0m4lfqxz9fps80000gn/T/AppTranslocation/590B87E8-BEDD-40D1-A770-7063B047F674/d/FreeCAD.app/Contents/Resources/Mod/CAM/Tools/Shape/endmill.fcstd
  Chipload = 0
  CuttingEdgeHeight = 10
  Diameter = 2.8
  Flutes = 0
  Length = 27
  Material = 0
  ShankDiameter = 3.17
  ShapeName = endmill
  SpindleDirection = 0
FEATURE [Path::FeaturePython] __8mm_Endmill006  label="2.8mm_Endmill002"  # Path/CAM operation (typed FeaturePython)
  HorizFeed = 3.33333
  HorizRapid = 0
  SpindleDir = 0
  SpindleSpeed = 2000
  Tool = -> ToolBit021
  ToolNumber = 12
  VertFeed = 3.33333
  VertRapid = 0
  expr: HorizRapid = SetupSheet001.HorizRapid
  expr: VertRapid = SetupSheet001.VertRapid
FEATURE [Part::FeaturePython] ToolBit022  label="3.0mm_Endmill003"  # Path/CAM toolbit (typed FeaturePython)
  BitPropertyNames = Chipload | CuttingEdgeHeight | Diameter | Flutes | Length | Material | ShankDiameter | SpindleDirection
  BitShape = /private/var/folders/4z/cpn_82wx3qz0m4lfqxz9fps80000gn/T/AppTranslocation/590B87E8-BEDD-40D1-A770-7063B047F674/d/FreeCAD.app/Contents/Resources/Mod/CAM/Tools/Shape/endmill.fcstd
  Chipload = 0
  CuttingEdgeHeight = 10
  Diameter = 3
  Flutes = 0
  Length = 27
  Material = 0
  ShankDiameter = 3.17
  ShapeName = endmill
  SpindleDirection = 0
FEATURE [Path::FeaturePython] __0mm_Endmill006  label="3.0mm_Endmill002"  # Path/CAM operation (typed FeaturePython)
  HorizFeed = 3.33333
  HorizRapid = 0
  SpindleDir = 0
  SpindleSpeed = 2000
  Tool = -> ToolBit022
  ToolNumber = 13
  VertFeed = 3.33333
  VertRapid = 0
  expr: HorizRapid = SetupSheet001.HorizRapid
  expr: VertRapid = SetupSheet001.VertRapid
FEATURE [Part::FeaturePython] ToolBit023  label="3.175mm_endmill011"  # Path/CAM toolbit (typed FeaturePython)
  BitPropertyNames = Chipload | CuttingEdgeHeight | Diameter | Flutes | Length | Material | ShankDiameter | SpindleDirection
  BitShape = /private/var/folders/4z/cpn_82wx3qz0m4lfqxz9fps80000gn/T/AppTranslocation/590B87E8-BEDD-40D1-A770-7063B047F674/d/FreeCAD.app/Contents/Resources/Mod/CAM/Tools/Shape/endmill.fcstd
  Chipload = 0
  CuttingEdgeHeight = 10
  Diameter = 3.17
  Flutes = 0
  Length = 27
  Material = 0
  ShankDiameter = 3.17
  ShapeName = endmill
  SpindleDirection = 0
FEATURE [Path::FeaturePython] __175mm_endmill008  label="3.175mm_endmill010"  # Path/CAM operation (typed FeaturePython)
  HorizFeed = 3.33333
  HorizRapid = 0
  SpindleDir = 0
  SpindleSpeed = 2000
  Tool = -> ToolBit023
  ToolNumber = 6
  VertFeed = 3.33333
  VertRapid = 0
  expr: HorizRapid = SetupSheet001.HorizRapid
  expr: VertRapid = SetupSheet001.VertRapid
FEATURE [App::DocumentObjectGroup] Tools001
  Group = -> [__8mm_Endmill004,__0mm_Endmill004,__2mm_endmill002,__4mm_Endmill003,__8mm_Endmill005,__0mm_Endmill005,__2mm_Endmill001,__4mm_Endmill004,__6mm_Endmill001,__8mm_Endmill006,__0mm_Endmill006,__175mm_endmill008]
FEATURE [Part::FeaturePython] Stock001  # WARN: FeaturePython — macro-defined, semantics opaque (R4)
  Base = -> Model001
  ExtXneg = 1
  ExtXpos = 1
  ExtYneg = 1
  ExtYpos = 1
  ExtZneg = 0
  ExtZpos = 0
  Placement = pos=(-78.2,-76.9,0) rot=(0,0,1;0rad)
  StockType = FromBase
FEATURE [Path::FeaturePython] MillFace  # Path/CAM operation (typed FeaturePython)
  Active = true
  AreaParams:
    Tolerance = 1e-07
    FitArcs = True
    Simplify = False
    CleanDistance = 0.0
    Accuracy = 0.01
    Unit = 1.0
    MinArcPoints = 4
    MaxArcPoints = 100
    ClipperScale = 10000000.0
    Fill = 0
    Coplanar = 0
    Reorient = True
    Outline = False
    Explode = False
    OpenMode = 0
    Deflection = 0.01
    SubjectFill = 0
    ClipFill = 0
    Offset = 0.0
    ExtraPass = 0
    Stepover = 0.0
    LastStepover = 0.0
    JoinType = 0
    EndType = 0
    MiterLimit = 2.0
    RoundPrecision = 0.0
    PocketMode = 2
    ToolRadius = 1.585
    PocketExtraOffset = 0.0
    PocketStepover = 0.317
    PocketLastStepover = 0.0
    FromCenter = True
    Angle = 45.0
    AngleShift = 0.0
    Shift = 0.0
    Thicken = False
    SectionCount = -1
    Stepdown = 1.0
    SectionOffset = 0.0
    SectionTolerance = 1e-06
    SectionMode = 2
    Project = False
  Base = -> [Body002]
  BoundaryShape = 0
  ClearEdges = false
  ClearanceHeight = 15
  CoolantMode = 0
  CutMode = 0
  CycleTime = 00:43:23
  ExcludeRaisedAreas = false
  ExtraOffset = 0
  FinalDepth = 10
  FinishDepth = 0
  KeepToolDown = false
  MinTravel = true
  OffsetPattern = 1
  OpFinalDepth = 10
  OpStartDepth = 13.17
  OpStockZMax = 10
  OpStockZMin = 0
  OpToolDiameter = 3.17
  PathParams = {'orientation': 1, 'feedrate': 3.3333333333333335, 'feedrate_v': 3.3333333333333335, 'verbose': True, 'resume_height': 13.0, 'retraction': 15.0, 'return_end': True, 'preamble': False}
  PocketLastStepOver = 0
  SafeHeight = 13
  SplitArcs = false
  StartAt = 0
  StartDepth = 10
  StartPoint = (0,0,0)
  StepDown = 3.17
  StepOver = 10
  ToolController = -> __175mm_endmill008
  UseRestMachining = false
  UseStartPoint = false
  ZigZagAngle = 45
  expr: ClearanceHeight = OpStockZMax + SetupSheet001.ClearanceHeightOffset
  expr: FinalDepth = OpFinalDepth
  expr: SafeHeight = OpStockZMax + SetupSheet001.SafeHeightOffset
  expr: StartDepth = 10
  expr: StepDown = OpToolDiameter
FEATURE [Path::FeaturePython] MillFace001  # Path/CAM operation (typed FeaturePython)
  Active = true
  AreaParams:
    Tolerance = 1e-07
    FitArcs = True
    Simplify = False
    CleanDistance = 0.0
    Accuracy = 0.01
    Unit = 1.0
    MinArcPoints = 4
    MaxArcPoints = 100
    ClipperScale = 10000000.0
    Fill = 0
    Coplanar = 0
    Reorient = True
    Outline = False
    Explode = False
    OpenMode = 0
    Deflection = 0.01
    SubjectFill = 0
    ClipFill = 0
    Offset = 0.0
    ExtraPass = 0
    Stepover = 0.0
    LastStepover = 0.0
    JoinType = 0
    EndType = 0
    MiterLimit = 2.0
    RoundPrecision = 0.0
    PocketMode = 2
    ToolRadius = 1.585
    PocketExtraOffset = 0.0
    PocketStepover = 0.317
    PocketLastStepover = 0.0
    FromCenter = True
    Angle = 45.0
    AngleShift = 0.0
    Shift = 0.0
    Thicken = False
    SectionCount = -1
    Stepdown = 1.0
    SectionOffset = 0.0
    SectionTolerance = 1e-06
    SectionMode = 2
    Project = False
  Base = -> [Body003]
  BoundaryShape = 0
  ClearEdges = false
  ClearanceHeight = 15
  CoolantMode = 0
  CutMode = 0
  CycleTime = 00:43:25
  ExcludeRaisedAreas = false
  ExtraOffset = 0
  FinalDepth = 10
  FinishDepth = 0
  KeepToolDown = false
  MinTravel = true
  OffsetPattern = 1
  OpFinalDepth = 10
  OpStartDepth = 13.17
  OpStockZMax = 10
  OpStockZMin = 0
  OpToolDiameter = 3.17
  PathParams = {'orientation': 1, 'feedrate': 3.3333333333333335, 'feedrate_v': 3.3333333333333335, 'verbose': True, 'resume_height': 13.0, 'retraction': 15.0, 'return_end': True, 'preamble': False}
  PocketLastStepOver = 0
  SafeHeight = 13
  SplitArcs = false
  StartAt = 0
  StartDepth = 10
  StartPoint = (0,0,0)
  StepDown = 3.17
  StepOver = 10
  ToolController = -> __175mm_endmill008
  UseRestMachining = false
  UseStartPoint = false
  ZigZagAngle = 45
  expr: ClearanceHeight = OpStockZMax + SetupSheet001.ClearanceHeightOffset
  expr: FinalDepth = OpFinalDepth
  expr: SafeHeight = OpStockZMax + SetupSheet001.SafeHeightOffset
  expr: StartDepth = 10
  expr: StepDown = OpToolDiameter
FEATURE [App::DocumentObjectGroup] Operations001
  Group = -> [MillFace,MillFace001]
FEATURE [Path::FeaturePython] Job001  # Path/CAM operation (typed FeaturePython)
  CycleTime = 01:26:48
  Fixtures = G54
  GeometryTolerance = 0.01
  JobType = 0
  Model = -> Model001
  Operations = -> Operations001
  OrderOutputBy = 0
  PostProcessor = 1
  SetupSheet = -> SetupSheet001
  SplitOutput = false
  Stock = -> Stock001
  Tools = -> Tools001
